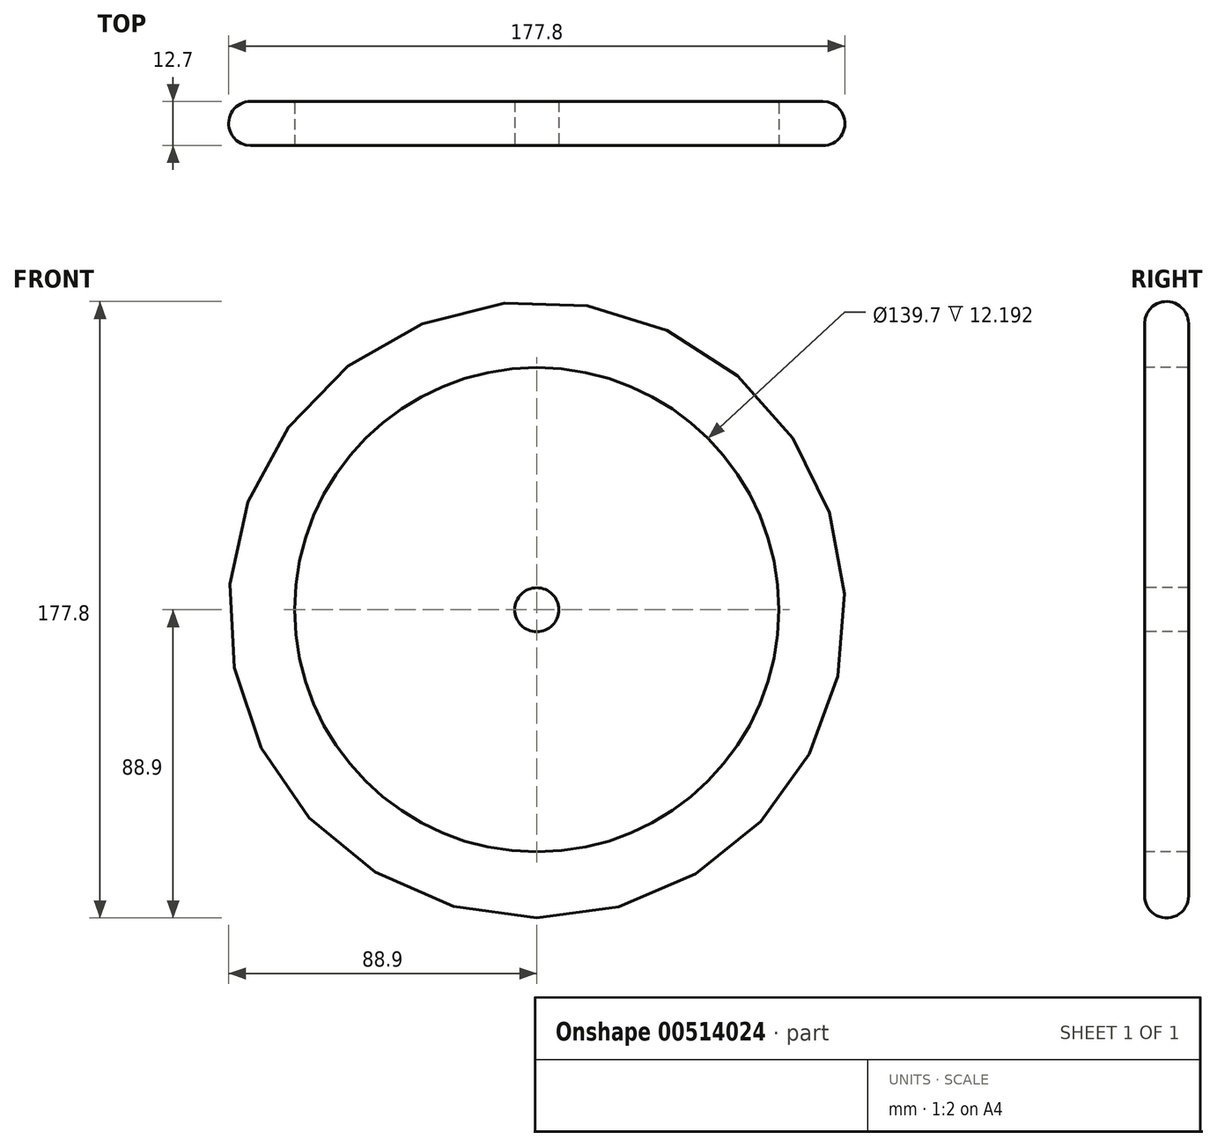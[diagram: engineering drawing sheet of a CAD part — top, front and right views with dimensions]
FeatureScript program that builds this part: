
annotation { "Feature Type Name" : "Feature", "Feature Type Description" : "" }
export const myFeature = defineFeature(function(context is Context, id is Id, definition is map)
    precondition{}
    {
        {
            var Q0;
            Q0=qCreatedBy(makeId("Front.planeOp"),FACE);
            var sketch = newSketch(context, id + "F0", { "sketchPlane" : qUnion([Q0])});
            skCircle(sketch, "E0", {"center": v(0, 0) * mm, "radius": 88.9 * mm});
            skSolve(sketch);
        }
        {
            var Q0;
            Q0=makeQuery(id+"F0.imprint","IMPRINT",FACE,{"disambiguationData":[TD([[makeQuery(id+"F0.imprint","IMPRINT",EDGE,{"derivedFrom":sQuery(id+"F0.wireOp",EDGE,"E0")}),1.0]])]});
            extrude(context, id + "F1", {"entities" : qUnion([Q0]), "depth" : 12.7 * mm, "offsetDistance" : 25.4 * mm});
        }
        {
            var Q0;
            Q0=makeQuery(id+"F1.opExtrude","CAP_FACE",FACE,{"disambiguationData":[OSD([sQuery(id+"F0.wireOp",EDGE,"E0")])],"isStart":false});
            var sketch = newSketch(context, id + "F2", { "sketchPlane" : qUnion([Q0])});
            skCircle(sketch, "E1", {"center": v(0, 0) * mm, "radius": 69.85 * mm});
            skCircle(sketch, "E2", {"center": v(0, 0) * mm, "radius": 6.35 * mm});
            skSolve(sketch);
        }
        {
            var Q0;
            Q0=makeQuery(id+"F2.imprint","IMPRINT",FACE,{"disambiguationData":[TD([[makeQuery(id+"F2.imprint","IMPRINT",EDGE,{"derivedFrom":sQuery(id+"F2.wireOp",EDGE,"E1")}),1.0]])]});
            extrude(context, id + "F3", {"entities" : qUnion([Q0]), "operationType" : NewBodyOperationType.REMOVE, "oppositeDirection" : true, "depth" : 25.4 * mm, "offsetDistance" : 25.4 * mm});
        }
        {
            var Q0;
            Q0=makeQuery(id+"F1.opExtrude","CAP_EDGE",EDGE,{"disambiguationData":[OSD([sQuery(id+"F0.wireOp",EDGE,"E0")])],"isStart":false});
            var Q1;
            Q1=makeQuery(id+"F1.opExtrude","CAP_EDGE",EDGE,{"disambiguationData":[OSD([sQuery(id+"F0.wireOp",EDGE,"E0")])],"isStart":true});
            fillet(context, id + "F4", {"entities" : qUnion([Q0, Q1]), "radius" : 6.35 * mm, "tangentPropagation" : true, "allowEdgeOverflow" : false});
        }
        {
            var Q0;
            Q0=makeQuery(id+"F3.boolean.opBoolean","INTERSECT",EDGE,{"derivedFrom":[makeQuery(id+"F1.opExtrude","CAP_FACE",FACE,{"disambiguationData":[OSD([sQuery(id+"F0.wireOp",EDGE,"E0")])],"isStart":true}),makeQuery(id+"F3.opExtrude","SWEPT_FACE",FACE,{"disambiguationData":[OSD([sQuery(id+"F2.wireOp",EDGE,"E1")])]})]});
            var Q1;
            Q1=makeQuery(id+"F3.boolean.opBoolean","COPY",EDGE,{"derivedFrom":makeQuery(id+"F3.opExtrude","CAP_EDGE",EDGE,{"disambiguationData":[OSD([sQuery(id+"F2.wireOp",EDGE,"E1")])],"isStart":true})});
            fillet(context, id + "F5", {"entities" : qUnion([Q0, Q1]), "radius" : 0.5 * mm, "tangentPropagation" : true, "allowEdgeOverflow" : false});
        }
    });
